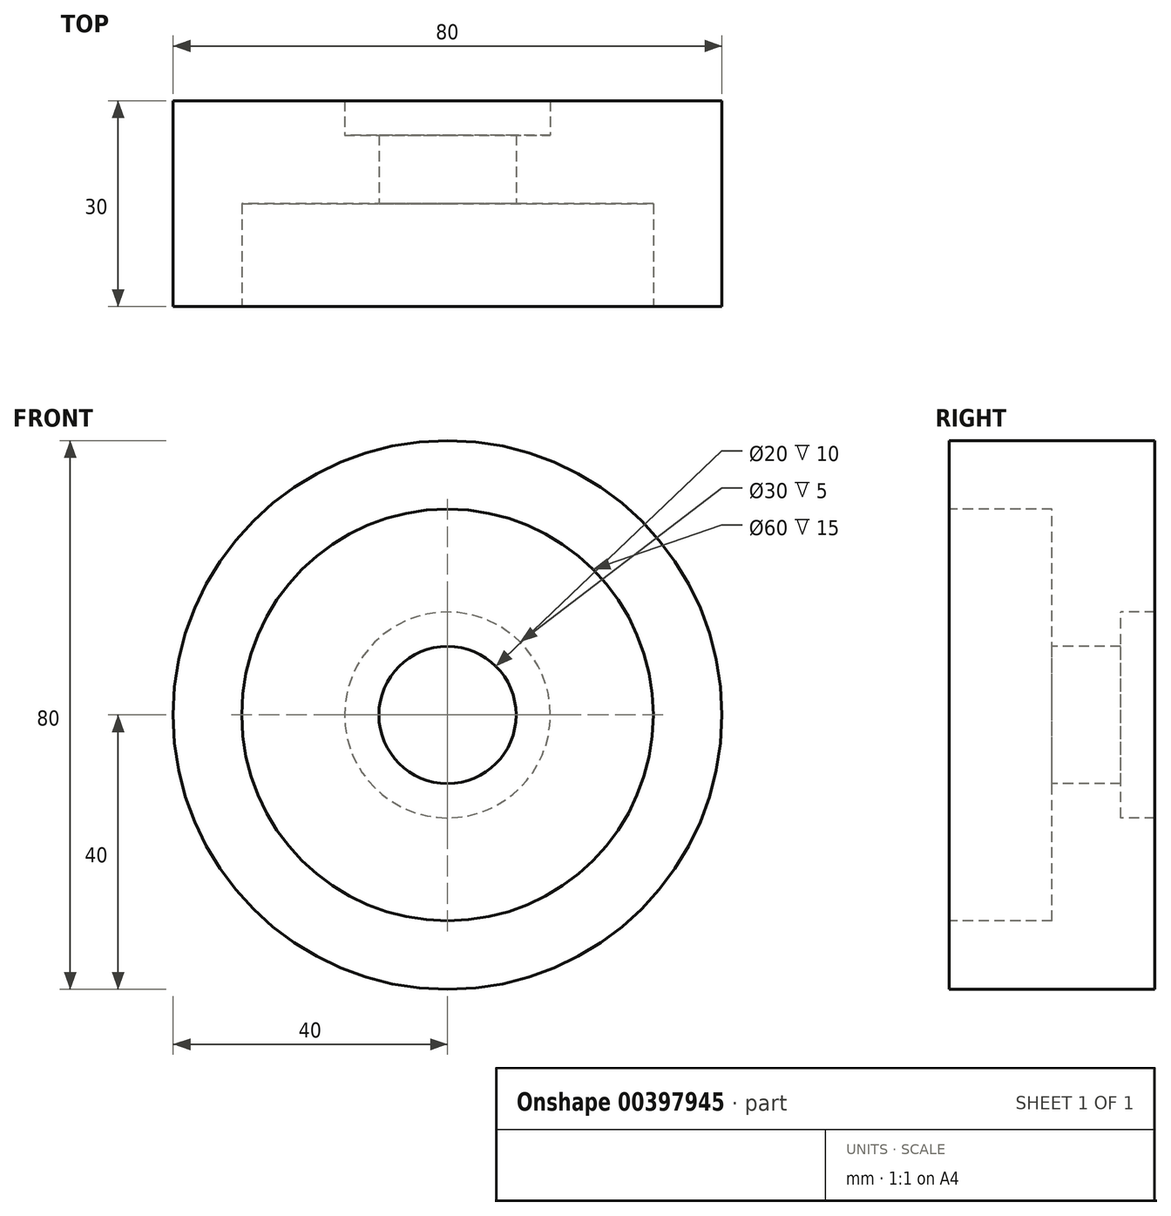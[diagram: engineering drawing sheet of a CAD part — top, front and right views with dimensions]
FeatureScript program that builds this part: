
annotation { "Feature Type Name" : "Feature", "Feature Type Description" : "" }
export const myFeature = defineFeature(function(context is Context, id is Id, definition is map)
    precondition{}
    {
        {
            var Q0;
            Q0=qCreatedBy(makeId("Right.planeOp"),FACE);
            var sketch = newSketch(context, id + "F0", { "sketchPlane" : qUnion([Q0])});
            skLineSegment(sketch, "E0", {"start": v(0, 10) * mm, "end": v(10, 10) * mm});
            skLineSegment(sketch, "E1", {"start": v(10, 10) * mm, "end": v(10, 15) * mm});
            skLineSegment(sketch, "E2", {"start": v(10, 15) * mm, "end": v(15, 15) * mm});
            skLineSegment(sketch, "E3", {"start": v(15, 15) * mm, "end": v(15, 40) * mm});
            skLineSegment(sketch, "E4", {"start": v(15, 40) * mm, "end": v(-15, 40) * mm});
            skLineSegment(sketch, "E5", {"start": v(-15, 40) * mm, "end": v(-15, 30) * mm});
            skLineSegment(sketch, "E6", {"start": v(-15, 30) * mm, "end": v(0, 30) * mm});
            skLineSegment(sketch, "E7", {"start": v(0, 30) * mm, "end": v(0, 10) * mm});
            skLineSegment(sketch, "E8", {"start": v(0, 0) * mm, "end": v(32.95, 0) * mm, "construction": true});
            skSolve(sketch);
        }
        {
            var Q0;
            Q0=makeQuery(id+"F0.imprint","IMPRINT",FACE,{"disambiguationData":[TD([[makeQuery(id+"F0.imprint","IMPRINT",EDGE,{"derivedFrom":sQuery(id+"F0.wireOp",EDGE,"E0")}),1.0]])]});
            var Q1;
            Q1=sQuery(id+"F0.wireOp",EDGE,"E8");
            revolve(context, id + "F1", {"entities" : qUnion([Q0]), "axis" : qUnion([Q1]), "revolveType" : RevolveType.FULL});
        }
    });
